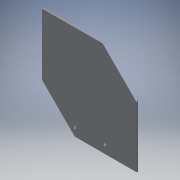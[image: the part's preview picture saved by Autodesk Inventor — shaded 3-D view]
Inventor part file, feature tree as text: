
AUTODESK INVENTOR PART (.ipt)
format: ipt  version: 2016 (Build 200138000, 138)  size: 99,328 bytes
history: native  units: in
note: dims shown in document units (in); Inventor stores cm internally (conversion verified against a paired STEP export)
features: extrude x2, sketch x2
ambient origin geometry x8: Origin, YZ Plane, XZ Plane, XY Plane, X Axis, Y Axis, Z Axis, Center Point
bodies: Solid1 (feature_tree)
feature tree (4):
  extrude  "Extrusion1"  Depth=8.0in
  extrude  "Extrusion2"  Depth=0.125in
  sketch  "Sketch1"  dims[d0=9.0in d1=8.0in]
  sketch  "Sketch2"  dims[d2=0.125in d3=0.0in d4=0.2656in d5=0.2656in d6=0.75in d7=0.75in d8=2.85in d9=3.075in d10=0.125in d11=0.0in]
